# Revit family: Head of Stair Louvre Vent
name_source: partatom
category: Generic Models
revit_build: Autodesk Revit 2018 (Build: 20190510_1515(x64)
units: mm (PartAtom-declared; Revit-internal decimal feet)

## family parameters
Always vertical = No
Can host rebar = No
Cut with Voids When Loaded = Yes
Host = Roof
Part Type = Normal
Room Calculation Point = No
Round Connector Dimension = Use Diameter
Shared = Yes

## types (1)
- 1m2 Head of Stairs louvre
    Assembly Code = Smokejet
    Blades Material = Metal
    Certification = CE EN12101-2
    Cost = 0 $
    Current = 1 A
    Date of Issue = 28.08.18
    Description = Roof mounted louvre vent designed to provide 1m2 free area
    Flange Length = 1150 mm
    Flange Width = 3265 mm  [stored 10.7119 ft]
    Geometric Free Area = At least 1.0 m2
    Height = 290 mm
    Length = 2815 mm  [stored 9.23556 ft]
    Main Material Metal = Powder Coated Aluminium RAL 9010
    Manufacturer = EMB
    Number of Blades = 21
    Revision = 1
    Weight = 100 kg
    Width = 700 mm  [stored 2.29659 ft]

note: [stored X ft] marks values corroborated as IEEE doubles in the binary element streams (Revit-internal decimal feet)

## geometry (parser evidence)
native form markers: Sweep x2
no freeform markers — native parametric forms only
